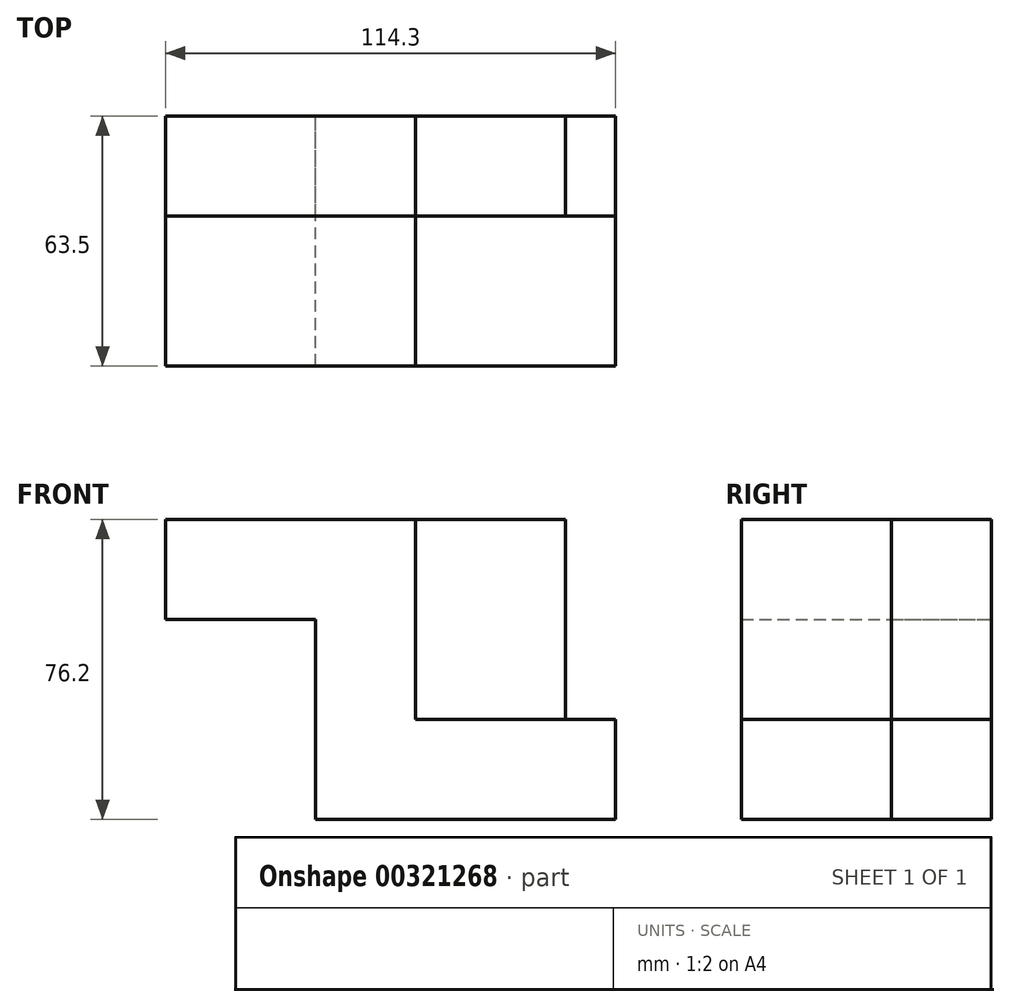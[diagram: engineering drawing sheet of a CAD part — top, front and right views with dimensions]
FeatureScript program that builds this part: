
annotation { "Feature Type Name" : "Feature", "Feature Type Description" : "" }
export const myFeature = defineFeature(function(context is Context, id is Id, definition is map)
    precondition{}
    {
        {
            var Q0;
            Q0=qCreatedBy(makeId("Front.planeOp"),FACE);
            var sketch = newSketch(context, id + "F0", { "sketchPlane" : qUnion([Q0])});
            skLineSegment(sketch, "E0", {"start": v(-46.61, 53.24) * mm, "end": v(-46.61, 27.84) * mm});
            skLineSegment(sketch, "E1", {"start": v(-46.61, 27.84) * mm, "end": v(-8.51, 27.84) * mm});
            skLineSegment(sketch, "E2", {"start": v(-8.51, 27.84) * mm, "end": v(-8.51, -22.96) * mm});
            skLineSegment(sketch, "E3", {"start": v(-8.51, -22.96) * mm, "end": v(67.69, -22.96) * mm});
            skLineSegment(sketch, "E4", {"start": v(67.69, -22.96) * mm, "end": v(67.69, 2.44) * mm});
            skLineSegment(sketch, "E5", {"start": v(67.69, 2.44) * mm, "end": v(16.89, 2.44) * mm});
            skLineSegment(sketch, "E6", {"start": v(16.89, 2.44) * mm, "end": v(16.89, 53.24) * mm});
            skLineSegment(sketch, "E7", {"start": v(16.89, 53.24) * mm, "end": v(-46.61, 53.24) * mm});
            skSolve(sketch);
        }
        {
            var Q0;
            Q0=makeQuery(id+"F0.imprint","IMPRINT",FACE,{"disambiguationData":[TD([[makeQuery(id+"F0.imprint","IMPRINT",EDGE,{"derivedFrom":sQuery(id+"F0.wireOp",EDGE,"E0")}),1.0]])]});
            extrude(context, id + "F1", {"entities" : qUnion([Q0]), "depth" : 63.5 * mm});
        }
        {
            var Q0;
            Q0 = qSketchRegion(id + "F0", true);
            extrude(context, id + "F2", {"entities" : qUnion([Q0]), "depth" : 25.4 * mm});
        }
        {
            var Q0;
            Q0=makeQuery(id+"F1.opExtrude","SWEPT_FACE",FACE,{"disambiguationData":[OSD([sQuery(id+"F0.wireOp",EDGE,"E6")])]});
            var sketch = newSketch(context, id + "F3", { "sketchPlane" : qUnion([Q0])});
            skLineSegment(sketch, "E8.bottom", {"start": v(0, 53.24) * mm, "end": v(-25.4, 53.24) * mm});
            skLineSegment(sketch, "E8.top", {"start": v(0, 2.44) * mm, "end": v(-25.4, 2.44) * mm});
            skLineSegment(sketch, "E8.left", {"start": v(0, 53.24) * mm, "end": v(0, 2.44) * mm});
            skLineSegment(sketch, "E8.right", {"start": v(-25.4, 53.24) * mm, "end": v(-25.4, 2.44) * mm});
            skSolve(sketch);
        }
        {
            var Q0;
            Q0=makeQuery(id+"F3.imprint","IMPRINT",FACE,{"disambiguationData":[TD([[makeQuery(id+"F3.imprint","IMPRINT",EDGE,{"derivedFrom":sQuery(id+"F3.wireOp",EDGE,"E8.bottom")}),-1.0]])]});
            extrude(context, id + "F4", {"entities" : qUnion([Q0]), "depth" : 38.1 * mm});
        }
    });
